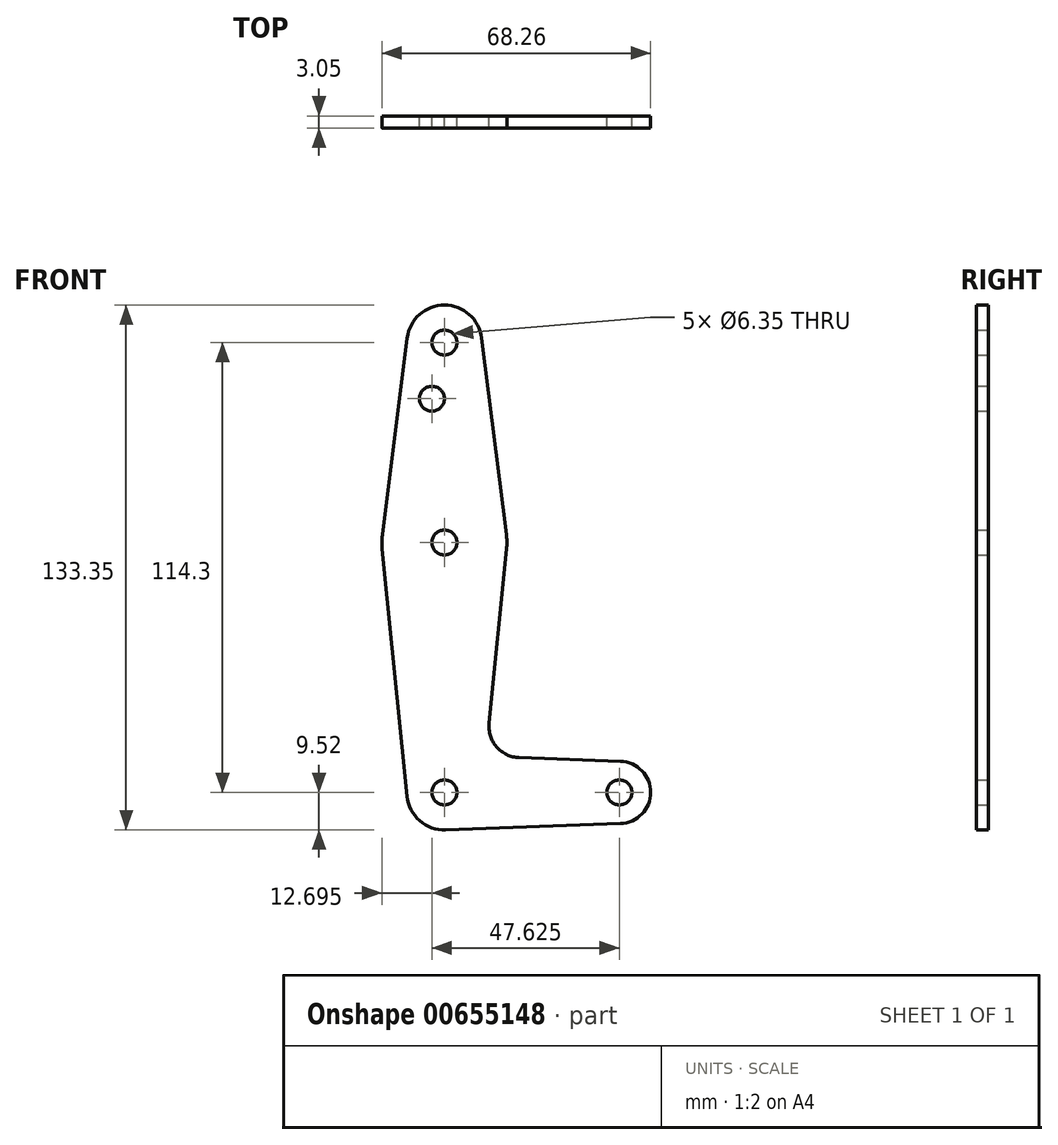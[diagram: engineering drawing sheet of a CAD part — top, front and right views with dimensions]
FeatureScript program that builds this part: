
annotation { "Feature Type Name" : "Feature", "Feature Type Description" : "" }
export const myFeature = defineFeature(function(context is Context, id is Id, definition is map)
    precondition{}
    {
        {
            var Q0;
            Q0=qCreatedBy(makeId("Front.planeOp"),FACE);
            var sketch = newSketch(context, id + "F0", { "sketchPlane" : qUnion([Q0])});
            skLineSegment(sketch, "E0", {"start": v(0, 0) * mm, "end": v(0, 114.3) * mm, "construction": true});
            skLineSegment(sketch, "E1", {"start": v(0, 0) * mm, "end": v(44.45, 0) * mm, "construction": true});
            skCircle(sketch, "E2", {"center": v(0, 114.3) * mm, "radius": 9.53 * mm});
            skCircle(sketch, "E3", {"center": v(0, 63.5) * mm, "radius": 15.88 * mm});
            skCircle(sketch, "E4", {"center": v(0, 0) * mm, "radius": 9.53 * mm});
            skCircle(sketch, "E5", {"center": v(44.45, 0) * mm, "radius": 7.94 * mm});
            skLineSegment(sketch, "E6", {"start": v(-9.45, 115.5) * mm, "end": v(-15.75, 65.48) * mm});
            skLineSegment(sketch, "E7", {"start": v(15.8, 61.91) * mm, "end": v(11.34, 17.6) * mm});
            skLineSegment(sketch, "E8", {"start": v(0.34, -9.52) * mm, "end": v(44.73, -7.93) * mm});
            skLineSegment(sketch, "E9", {"start": v(18.97, 8.85) * mm, "end": v(44.73, 7.93) * mm});
            skLineSegment(sketch, "E10", {"start": v(9.45, 115.5) * mm, "end": v(15.75, 65.48) * mm});
            skLineSegment(sketch, "E11", {"start": v(-15.8, 61.91) * mm, "end": v(-9.48, -0.95) * mm});
            skCircle(sketch, "E12", {"center": v(-3.18, 100.03) * mm, "radius": 3.18 * mm});
            skCircle(sketch, "E13", {"center": v(0, 114.3) * mm, "radius": 3.18 * mm});
            skCircle(sketch, "E14", {"center": v(0, 63.5) * mm, "radius": 3.18 * mm});
            skCircle(sketch, "E15", {"center": v(0, 0) * mm, "radius": 3.18 * mm});
            skCircle(sketch, "E16", {"center": v(44.45, 0) * mm, "radius": 3.18 * mm});
            skArc(sketch, "E17.filletArc", {"start": v(11.34, 17.6) * mm, "mid": v(13.26, 11.57) * mm, "end": v(18.97, 8.85) * mm});
            skSolve(sketch);
        }
        {
            var Q0;
            Q0 = qSketchRegion(id + "F0", true);
            extrude(context, id + "F1", {"entities" : qUnion([Q0]), "depth" : 3.05 * mm, "offsetDistance" : 25.4 * mm});
        }
    });
